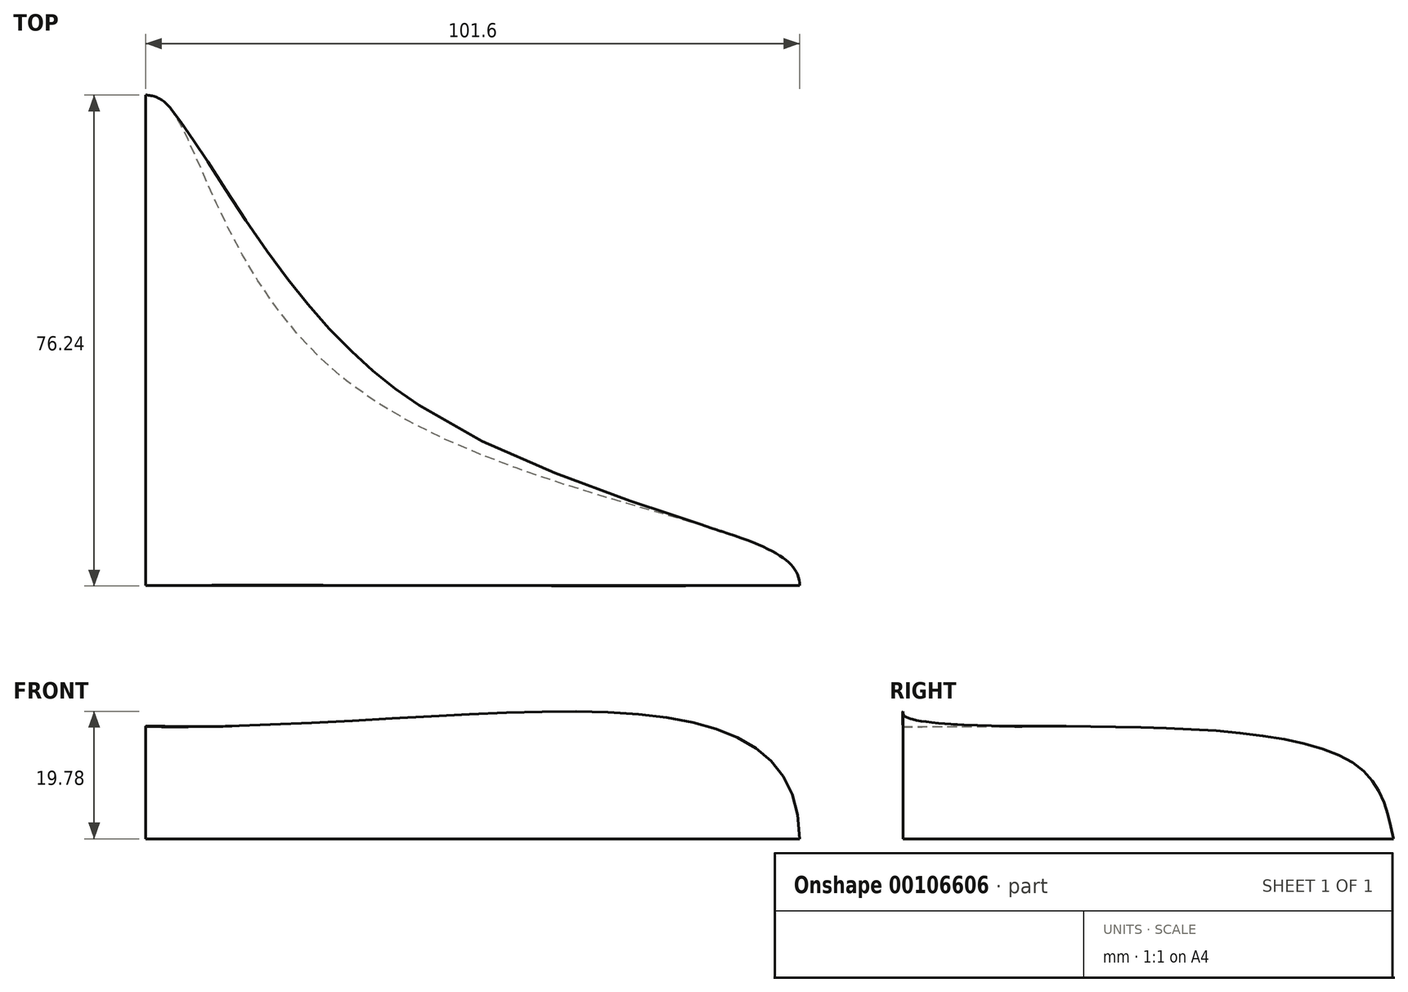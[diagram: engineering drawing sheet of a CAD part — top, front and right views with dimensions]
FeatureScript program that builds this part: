
annotation { "Feature Type Name" : "Feature", "Feature Type Description" : "" }
export const myFeature = defineFeature(function(context is Context, id is Id, definition is map)
    precondition{}
    {
        {
            var Q0;
            Q0=qCreatedBy(makeId("Top.planeOp"),FACE);
            var sketch = newSketch(context, id + "F0", { "sketchPlane" : qUnion([Q0])});
            skLineSegment(sketch, "E0.bottom", {"start": v(101.6, -76.2) * mm, "end": v(-101.6, -76.2) * mm, "construction": true});
            skLineSegment(sketch, "E0.top", {"start": v(101.6, 76.2) * mm, "end": v(-101.6, 76.2) * mm, "construction": true});
            skLineSegment(sketch, "E0.left", {"start": v(101.6, -76.2) * mm, "end": v(101.6, 76.2) * mm, "construction": true});
            skLineSegment(sketch, "E0.right", {"start": v(-101.6, -76.2) * mm, "end": v(-101.6, 76.2) * mm, "construction": true});
            skPoint(sketch, "E0.middle", {"position": v(0, 0) * mm});
            skLineSegment(sketch, "E1", {"start": v(-101.6, 0) * mm, "end": v(101.6, 0) * mm, "construction": true});
            skLineSegment(sketch, "E2", {"start": v(0, 76.2) * mm, "end": v(0, -76.2) * mm, "construction": true});
            skLineSegment(sketch, "E3.0", {"start": v(-101.6, 6.35) * mm, "end": v(101.6, 6.35) * mm, "construction": true});
            skLineSegment(sketch, "E4.0", {"start": v(-6.35, 76.2) * mm, "end": v(-6.35, -76.2) * mm, "construction": true});
            skLineSegment(sketch, "E5.0", {"start": v(101.6, 69.85) * mm, "end": v(-101.6, 69.85) * mm, "construction": true});
            skLineSegment(sketch, "E6.0", {"start": v(-95.25, -76.2) * mm, "end": v(-95.25, 76.2) * mm, "construction": true});
            skFitSpline(sketch, "E7", {"points": [v(-101.6, 0) * mm, v(-95.25, 6.35) * mm, v(-31.73, 31.38) * mm, v(-6.35, 69.85) * mm, v(0, 76.2) * mm], "startDerivative": vector(0, 54) * mm, "endDerivative": vector(60.48, 0) * mm});
            skFitSpline(sketch, "E8.MirrorCS", {"points": [v(101.6, 0) * mm, v(95.25, 6.35) * mm, v(31.73, 31.38) * mm, v(6.35, 69.85) * mm, v(0, 76.2) * mm], "startDerivative": vector(0, 54) * mm, "endDerivative": vector(-60.48, 0) * mm});
            skLineSegment(sketch, "E9", {"start": v(101.6, 0) * mm, "end": v(-101.6, 0) * mm});
            skLineSegment(sketch, "E10", {"start": v(0, 0) * mm, "end": v(0, 76.2) * mm});
            skSolve(sketch);
        }
        {
            var Q0;
            Q0=qCreatedBy(makeId("Front.planeOp"),FACE);
            var sketch = newSketch(context, id + "F1", { "sketchPlane" : qUnion([Q0])});
            skPoint(sketch, "E11.0", {"position": v(101.6, 0) * mm});
            skPoint(sketch, "E12.0", {"position": v(-101.6, 0) * mm});
            skLineSegment(sketch, "E13", {"start": v(-101.6, 0) * mm, "end": v(-101.6, 19.05) * mm, "construction": true});
            skLineSegment(sketch, "E14", {"start": v(101.6, 0) * mm, "end": v(-101.6, 0) * mm});
            skFitSpline(sketch, "E15", {"points": [v(0, 17.43) * mm, v(101.6, 0) * mm], "startDerivative": vector(148.66, -2.4) * mm, "endDerivative": vector(0, -90.51) * mm});
            skLineSegment(sketch, "E16", {"start": v(0, 17.43) * mm, "end": v(0, 0) * mm});
            skSolve(sketch);
        }
        {
            var Q0;
            Q0=qCreatedBy(makeId("Right.planeOp"),FACE);
            var sketch = newSketch(context, id + "F2", { "sketchPlane" : qUnion([Q0])});
            skPoint(sketch, "E17.0", {"position": v(76.2, 0) * mm});
            skPoint(sketch, "E18.0", {"position": v(0, 17.43) * mm});
            skFitSpline(sketch, "E19", {"points": [v(0, 17.43) * mm, v(2.1, 17.43) * mm, v(30.05, 17.43) * mm, v(70.28, 11.57) * mm, v(76.2, 0) * mm], "startDerivative": vector(17.77, -0.1) * mm, "endDerivative": vector(12.34, -60.35) * mm});
            skLineSegment(sketch, "E20", {"start": v(0, 17.43) * mm, "end": v(0, 0) * mm});
            skLineSegment(sketch, "E21", {"start": v(0, 0) * mm, "end": v(76.2, 0) * mm});
            skSolve(sketch);
        }
        {
            var Q0;
            {var subQ0=sQuery(id+"F0.wireOp",EDGE,"E8.MirrorCS");Q0=makeQuery(id+"F0.imprint","IMPRINT",FACE,{"disambiguationData":[TD([[makeQuery(id+"F0.imprint","IMPRINT",EDGE,{"derivedFrom":subQ0}),1.0]])]});}
            var Q1;
            Q1=sQuery(id+"F1.wireOp",EDGE,"E15");
            var Q2;
            Q2=sQuery(id+"F0.wireOp",EDGE,"E8.MirrorCS");
            var Q3;
            Q3=sQuery(id+"F2.wireOp",EDGE,"E19");
            loft(context, id + "F3", {"bodyType" : ToolBodyType.SURFACE, "addGuides" : true, "sheetProfilesArray" : [{ "sheetProfileEntities" : qUnion([Q0]) }], "wireProfilesArray" : [{ "wireProfileEntities" : qUnion([Q1]) }, { "wireProfileEntities" : qUnion([Q2]) }], "guidesArray" : [{ "guideEntities" : qUnion([Q3]), "guideDerivativeType" : LoftGuideDerivativeType.DEFAULT, "guideDerivativeMagnitude" : 1 }]});
        }
    });
